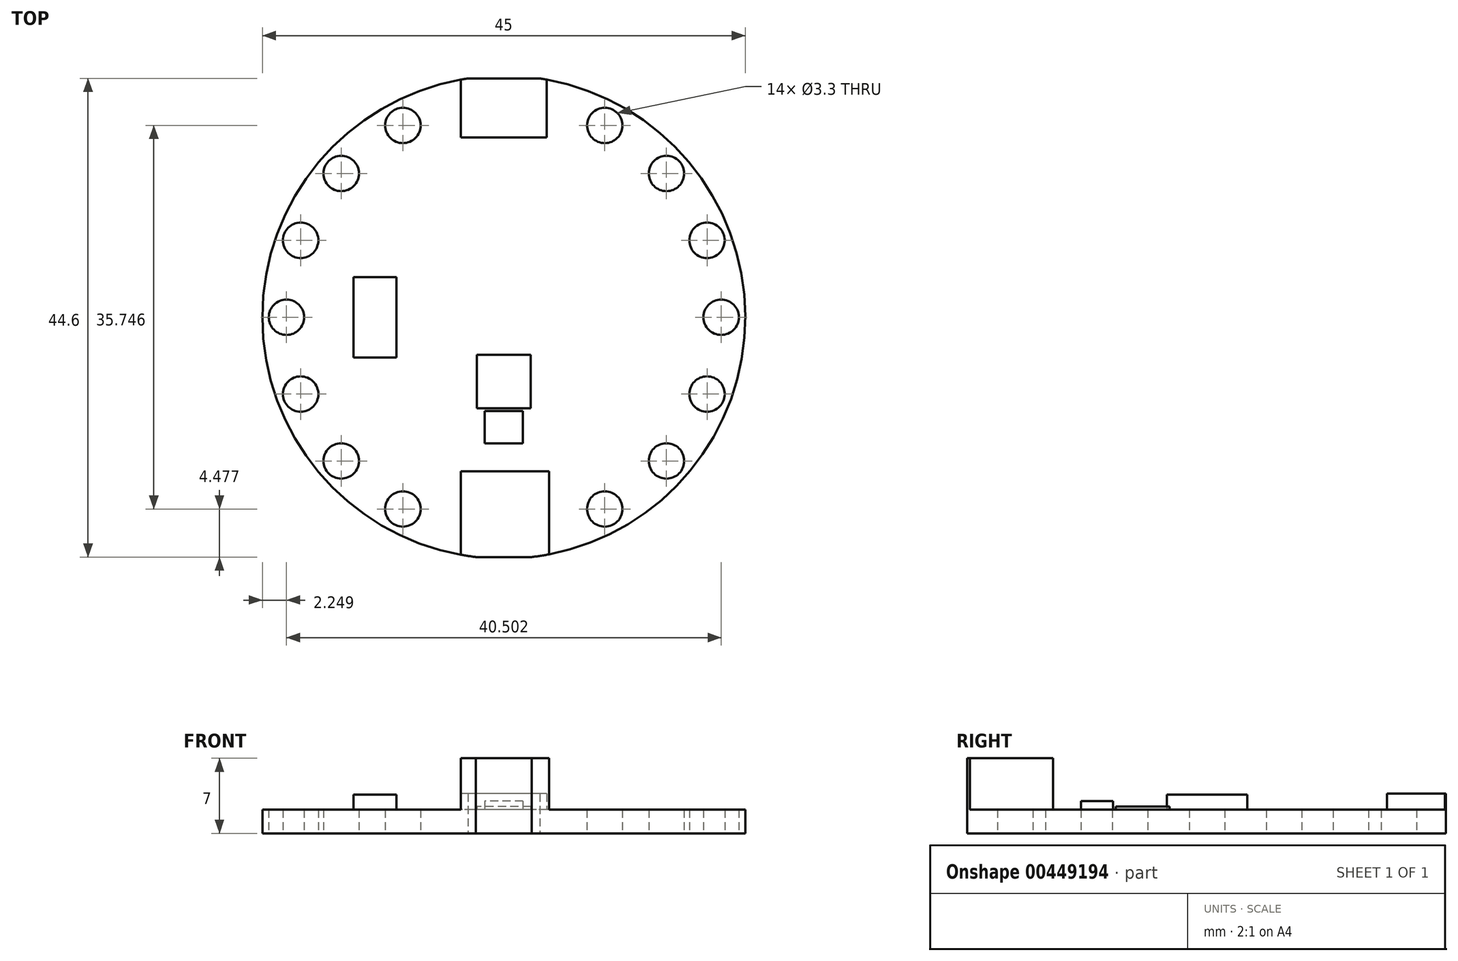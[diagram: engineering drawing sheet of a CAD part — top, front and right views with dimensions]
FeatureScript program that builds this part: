
annotation { "Feature Type Name" : "Feature", "Feature Type Description" : "" }
export const myFeature = defineFeature(function(context is Context, id is Id, definition is map)
    precondition{}
    {
        {
            var Q0;
            Q0=qCreatedBy(makeId("Top.planeOp"),FACE);
            var sketch = newSketch(context, id + "F0", { "sketchPlane" : qUnion([Q0])});
            skCircle(sketch, "E0", {"center": v(0, 0) * mm, "radius": 22.5 * mm});
            skCircle(sketch, "E1", {"center": v(20.25, 0) * mm, "radius": 1.65 * mm});
            skCircle(sketch, "E2.1.0", {"center": v(18.93, -7.17) * mm, "radius": 1.65 * mm});
            skCircle(sketch, "E2.2.0", {"center": v(15.15, -13.4) * mm, "radius": 1.65 * mm});
            skCircle(sketch, "E2.3.0", {"center": v(9.4, -17.87) * mm, "radius": 1.65 * mm});
            skPoint(sketch, "E2.center", {"position": v(0.1, 0) * mm});
            skLineSegment(sketch, "E2.anchor1", {"start": v(0.1, 0) * mm, "end": v(20.25, 0) * mm, "construction": true});
            skLineSegment(sketch, "E2.anchor2", {"start": v(0.1, 0) * mm, "end": v(9.4, -17.87) * mm, "construction": true});
            skCircle(sketch, "E3.MirrorC", {"center": v(9.4, 17.87) * mm, "radius": 1.65 * mm});
            skCircle(sketch, "E4.MirrorC", {"center": v(15.15, 13.4) * mm, "radius": 1.65 * mm});
            skCircle(sketch, "E5.MirrorC", {"center": v(18.93, 7.17) * mm, "radius": 1.65 * mm});
            skCircle(sketch, "E6.MirrorC", {"center": v(-20.25, 0) * mm, "radius": 1.65 * mm});
            skCircle(sketch, "E7.MirrorC", {"center": v(-18.93, 7.17) * mm, "radius": 1.65 * mm});
            skCircle(sketch, "E8.MirrorC", {"center": v(-15.15, 13.4) * mm, "radius": 1.65 * mm});
            skCircle(sketch, "E9.MirrorC", {"center": v(-18.93, -7.17) * mm, "radius": 1.65 * mm});
            skCircle(sketch, "E10.MirrorC", {"center": v(-15.15, -13.4) * mm, "radius": 1.65 * mm});
            skCircle(sketch, "E11.MirrorC", {"center": v(-9.4, -17.87) * mm, "radius": 1.65 * mm});
            skCircle(sketch, "E12.MirrorC", {"center": v(-9.4, 17.87) * mm, "radius": 1.65 * mm});
            skLineSegment(sketch, "E13.bottom", {"start": v(4, 22.25) * mm, "end": v(-4, 22.25) * mm});
            skLineSegment(sketch, "E13.top", {"start": v(4, 16.75) * mm, "end": v(-4, 16.75) * mm});
            skLineSegment(sketch, "E13.left", {"start": v(4, 22.25) * mm, "end": v(4, 16.75) * mm});
            skLineSegment(sketch, "E13.right", {"start": v(-4, 22.25) * mm, "end": v(-4, 16.75) * mm});
            skPoint(sketch, "E13.middle", {"position": v(0, 19.5) * mm});
            skLineSegment(sketch, "E14.bottom", {"start": v(4.2, -22.35) * mm, "end": v(-4, -22.35) * mm});
            skLineSegment(sketch, "E14.top", {"start": v(4.2, -14.35) * mm, "end": v(-4, -14.35) * mm});
            skLineSegment(sketch, "E14.left", {"start": v(4.2, -22.35) * mm, "end": v(4.2, -14.35) * mm});
            skLineSegment(sketch, "E14.right", {"start": v(-4, -22.35) * mm, "end": v(-4, -14.35) * mm});
            skPoint(sketch, "E14.middle", {"position": v(0, -18.35) * mm});
            skLineSegment(sketch, "E15.bottom", {"start": v(-10, -3.75) * mm, "end": v(-14, -3.75) * mm});
            skLineSegment(sketch, "E15.top", {"start": v(-10, 3.75) * mm, "end": v(-14, 3.75) * mm});
            skLineSegment(sketch, "E15.left", {"start": v(-10, -3.75) * mm, "end": v(-10, 3.75) * mm});
            skLineSegment(sketch, "E15.right", {"start": v(-14, -3.75) * mm, "end": v(-14, 3.75) * mm});
            skPoint(sketch, "E15.middle", {"position": v(-12, 0) * mm});
            skLineSegment(sketch, "E16.bottom", {"start": v(2.5, -8.5) * mm, "end": v(-2.5, -8.5) * mm});
            skLineSegment(sketch, "E16.top", {"start": v(2.5, -3.5) * mm, "end": v(-2.5, -3.5) * mm});
            skLineSegment(sketch, "E16.left", {"start": v(2.5, -8.5) * mm, "end": v(2.5, -3.5) * mm});
            skLineSegment(sketch, "E16.right", {"start": v(-2.5, -8.5) * mm, "end": v(-2.5, -3.5) * mm});
            skPoint(sketch, "E16.middle", {"position": v(0, -6) * mm});
            skLineSegment(sketch, "E17.bottom", {"start": v(1.78, -11.75) * mm, "end": v(-1.78, -11.75) * mm});
            skLineSegment(sketch, "E17.top", {"start": v(1.78, -8.75) * mm, "end": v(-1.78, -8.75) * mm});
            skLineSegment(sketch, "E17.left", {"start": v(1.78, -11.75) * mm, "end": v(1.78, -8.75) * mm});
            skLineSegment(sketch, "E17.right", {"start": v(-1.78, -11.75) * mm, "end": v(-1.78, -8.75) * mm});
            skPoint(sketch, "E17.middle", {"position": v(0, -10.25) * mm});
            skSolve(sketch);
        }
        {
            var Q0;
            Q0=makeQuery(id+"F0.imprint","IMPRINT",FACE,{"disambiguationData":[TD([[makeQuery(id+"F0.imprint","IMPRINT",EDGE,{"derivedFrom":sQuery(id+"F0.wireOp",EDGE,"E2.1.0")}),-1.0]])]});
            extrude(context, id + "F1", {"entities" : qUnion([Q0]), "depth" : 2.2 * mm});
        }
        {
            var Q0;
            {var subQ6=sQuery(id+"F0.wireOp",EDGE,"E13.top");Q0=makeQuery(id+"F0.imprint","IMPRINT",FACE,{"disambiguationData":[TD([[makeQuery(id+"F0.imprint","IMPRINT",EDGE,{"derivedFrom":subQ6}),-1.0]])]});}
            extrude(context, id + "F2", {"entities" : qUnion([Q0]), "operationType" : NewBodyOperationType.ADD, "depth" : 3.7 * mm});
        }
        {
            var Q0;
            {var subQ0=sQuery(id+"F0.wireOp",EDGE,"E14.top");Q0=makeQuery(id+"F0.imprint","IMPRINT",FACE,{"disambiguationData":[TD([[makeQuery(id+"F0.imprint","IMPRINT",EDGE,{"derivedFrom":subQ0}),1.0]])]});}
            extrude(context, id + "F3", {"entities" : qUnion([Q0]), "operationType" : NewBodyOperationType.ADD, "depth" : 7 * mm});
        }
        {
            var Q0;
            Q0=makeQuery(id+"F0.imprint","IMPRINT",FACE,{"disambiguationData":[TD([[makeQuery(id+"F0.imprint","IMPRINT",EDGE,{"derivedFrom":sQuery(id+"F0.wireOp",EDGE,"E15.bottom")}),-1.0]])]});
            extrude(context, id + "F4", {"entities" : qUnion([Q0]), "operationType" : NewBodyOperationType.ADD, "depth" : 3.6 * mm});
        }
        {
            var Q0;
            Q0=makeQuery(id+"F0.imprint","IMPRINT",FACE,{"disambiguationData":[TD([[makeQuery(id+"F0.imprint","IMPRINT",EDGE,{"derivedFrom":sQuery(id+"F0.wireOp",EDGE,"E16.bottom")}),-1.0]])]});
            extrude(context, id + "F5", {"entities" : qUnion([Q0]), "operationType" : NewBodyOperationType.ADD, "depth" : 2.5 * mm});
        }
        {
            var Q0;
            Q0=makeQuery(id+"F0.imprint","IMPRINT",FACE,{"disambiguationData":[TD([[makeQuery(id+"F0.imprint","IMPRINT",EDGE,{"derivedFrom":sQuery(id+"F0.wireOp",EDGE,"E17.bottom")}),-1.0]])]});
            extrude(context, id + "F6", {"entities" : qUnion([Q0]), "operationType" : NewBodyOperationType.ADD, "depth" : 3 * mm});
        }
    });
